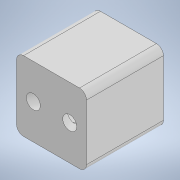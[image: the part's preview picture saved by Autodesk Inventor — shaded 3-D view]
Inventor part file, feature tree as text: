
AUTODESK INVENTOR PART (.ipt)
format: ipt  version: 2022 (Build 260153000, 153)  size: 19,077,120 bytes
history: native  units: mm
features: sketch x5, extrude x3, projected_geometry x3, other x1, move_body x1, revolve x1, sweep x1, pattern_circular x1, fillet x1, hole x1, chamfer x1, draft x1
ambient origin geometry x8: Origin, YZ Plane, XZ Plane, XY Plane, X Axis, Y Axis, Z Axis, Center Point
bodies: Solid1 (feature_tree), Solid2 (feature_tree)
feature tree (20):
  other  "MeshFeature1"
  move_body  "Move Body1"
  sketch  "Sketch1"  dims[d0=-263.204mm d1=-210.1mm d2=-54.192mm d3=5.0mm]
  extrude  "Extrusion1"  Depth=5.0mm
  revolve  "Revolution1"  [1 undecoded]
  sweep  "Sweep1"
  extrude  "Extrusion2"  Depth=40.0mm TaperAngle=0.0deg
  pattern_circular  "Circular Pattern1"  [2 undecoded]
  fillet  "Fillet1"  [1 undecoded]
  hole  "Hole1"  [1 undecoded]
  extrude  "Extrusion3"  Depth=2.0mm TaperAngle=360.0deg
  chamfer  "Chamfer1"  Distance=4.0mm
  draft  "FaceDraft1"
  sketch  "Sketch2"  dims[d4=8.0mm d5=30.0mm]
  sketch  "Sketch3"  dims[d6=16.0mm d7=39.0mm]
  projected_geometry  "Projected Loop1"
  sketch  "Sketch4"  dims[d8=40.0mm d9=40.0mm d10=0.0mm]
  projected_geometry  "Projected Loop2"
  sketch  "Sketch5"  dims[d11=90.0deg d12=8.0mm d13=0.0mm d14=0.0mm d15=4.0mm d16=0.0mm d17=20.0mm d18=360.0deg d20=4.0mm d21=4.0mm d22=6.0mm d23=4.0mm d24=2.0mm d25=90.0deg d26=14.0mm d27=0.0mm d28=4.0mm d29=0.0mm d30=1.0mm d31=2.0mm d32=45.0deg d33=0.349066mm]
  projected_geometry  "Projected Loop3"
note: 5 required parameter values undecoded (feature->parameter linkage not recoverable at this tier; creation-order binding heuristic only, values carry confidence <= 0.55)